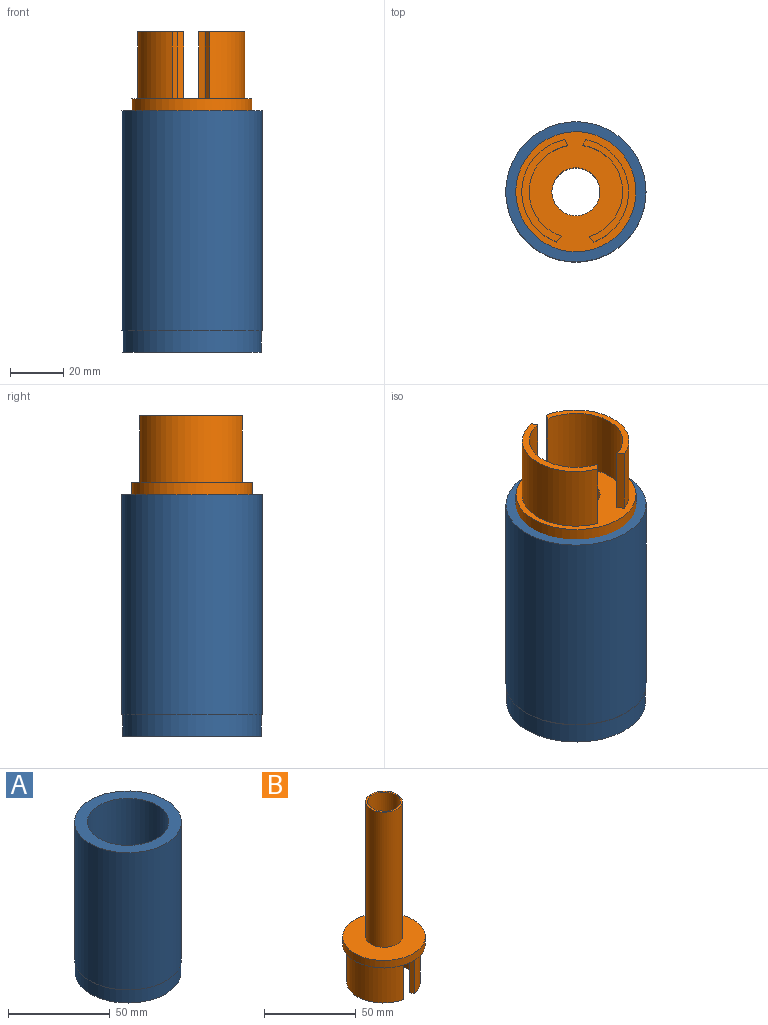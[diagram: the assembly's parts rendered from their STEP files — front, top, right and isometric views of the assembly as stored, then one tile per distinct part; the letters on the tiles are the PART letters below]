
ASSEMBLY  parts=2 mates=1
PART A: 14 faces, bbox 52.5x52.5x90.5 mm
  f0: plane 14x3.5mm, normal (0,0,1), area 33.7mm2, adj f2,f3,f4,f5
  f1: plane 8x3mm, normal (0,0,1), area 18.4mm2, adj f5,f6,f7,f8
  f2: plane 8x2.24mm, normal (-0.75,-0.67,0), area 24mm2, adj f0,f3,f5,f10
  f3: cylinder r=17.12mm len=10mm, axis (0,0,-1), area 81.2mm2, adj f0,f2,f4,f10
  f4: plane 8x2.24mm, normal (0.75,-0.67,0), area 24mm2, adj f0,f3,f5,f10
  f5: cylinder r=20mm len=90.5mm, axis (0,0,-1), area 11193.7mm2, adj f0,f1,f2,f4,f6,f8,f10,f13
  f6: plane 8x2.6mm, normal (0.87,0.5,0), area 24mm2, adj f1,f5,f7,f10
  f7: cylinder r=17.09mm len=8mm, axis (0,0,-1), area 40.1mm2, adj f1,f6,f8,f10
  f8: plane 8x2.6mm, normal (-0.87,0.5,0), area 24mm2, adj f1,f5,f7,f10
  f9: cylinder r=26mm len=52mm, axis (0,0,-1), area 1306.9mm2, adj f10,f11
  f10: plane 52x52mm, normal (0,0,-1), area 919.2mm2, adj f2,f3,f4,f5,f6,f7,f8,f9
  f11: plane 52.5x52.5mm, normal (0,0,-1), area 41mm2, adj f9,f12
  f12: cylinder r=26.25mm len=82.5mm, axis (0,0,-1), area 13607mm2, adj f11,f13
  f13: plane 52.5x52.5mm, normal (0,0,1), area 908.1mm2, adj f5,f12
PART B: 16 faces, bbox 45x45x120 mm
  f0: cylinder r=17.5mm len=34.13mm, axis (0,0,1), area 1188.6mm2, adj f1,f2,f12,f14
  f1: plane 38.33x17.25mm, normal (0,0,-1), area 113.4mm2, adj f0,f12,f13,f14
  f2: plane 45x45mm, normal (0,0,-1), area 1089.8mm2, adj f0,f3,f6,f8,f10,f11,f12,f13
  f3: cylinder r=9mm len=95mm, axis (0,0,-1), area 5372.1mm2, adj f2,f5
  f4: cylinder r=10mm len=90mm, axis (0,0,-1), area 5654.9mm2, adj f5,f7
  f5: plane 20x20mm, normal (0,0,1), area 59.7mm2, adj f3,f4
  f6: cylinder r=22.5mm len=45mm, axis (0,0,1), area 706.9mm2, adj f2,f7
  f7: plane 45x45mm, normal (0,0,1), area 1276.3mm2, adj f4,f6
  f8: cylinder r=17.5mm len=33.91mm, axis (0,0,1), area 1163.8mm2, adj f2,f9,f11,f15
  f9: plane 38.33x17.3mm, normal (0,0,-1), area 132.7mm2, adj f8,f10,f11,f15
  f10: cylinder r=20mm len=38.33mm, axis (0,0,1), area 1291.3mm2, adj f2,f9,f11,f15
  f11: plane 25x2.17mm, normal (0.75,0.67,0), area 72.8mm2, adj f2,f8,f9,f10
  f12: plane 25x2.04mm, normal (-0.75,0.67,0), area 68.3mm2, adj f0,f1,f2,f13
  f13: cylinder r=20mm len=38.33mm, axis (0,0,1), area 1291.3mm2, adj f1,f2,f12,f14
  f14: plane 25x2.17mm, normal (-0.87,-0.5,0), area 62.6mm2, adj f0,f1,f2,f13
  f15: plane 25x2.25mm, normal (0.87,-0.5,0), area 65mm2, adj f2,f8,f9,f10
PLACE A t=(-72.09,-31.24,-38.63)mm
PLACE B rot(axis=(1,0,0),180deg) t=(-72.09,-31.24,51.37)mm
MATE fastened B.f0 <-> A.f5  axis (0,0,-1) through (-72.09,-31.24,-38.63)mm
